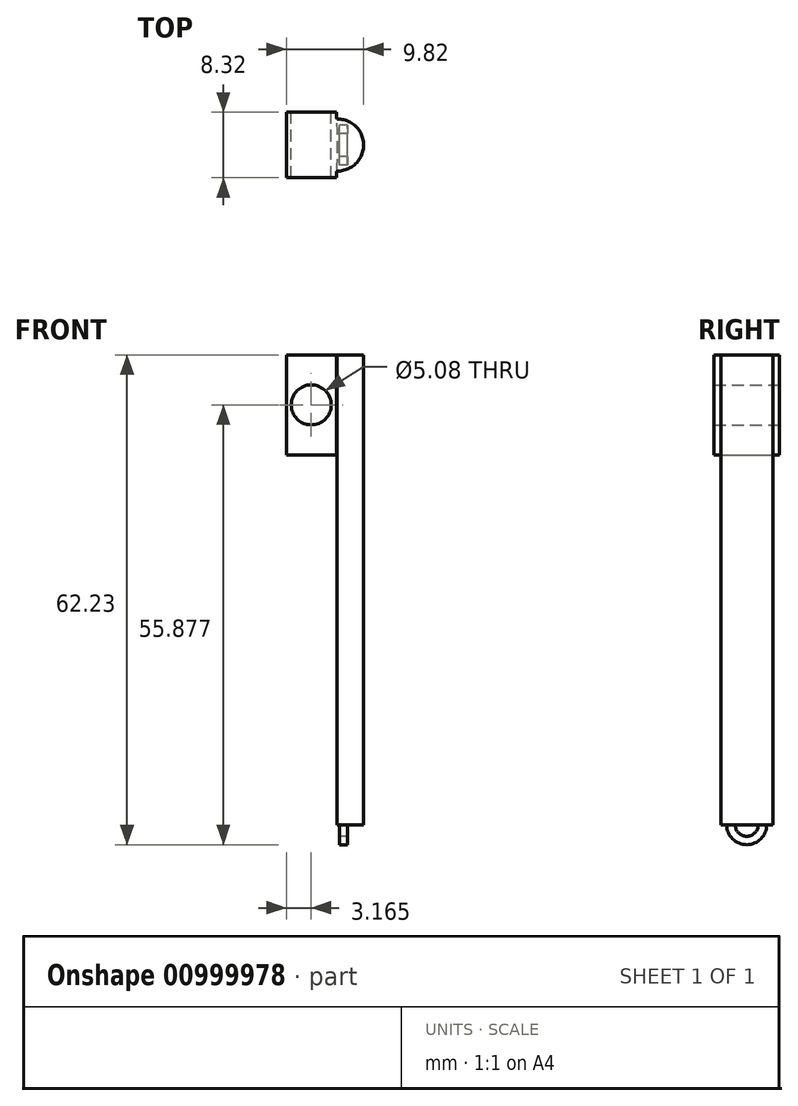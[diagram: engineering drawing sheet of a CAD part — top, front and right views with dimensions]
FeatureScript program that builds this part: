
annotation { "Feature Type Name" : "Feature", "Feature Type Description" : "" }
export const myFeature = defineFeature(function(context is Context, id is Id, definition is map)
    precondition{}
    {
        {
            var Q0;
            Q0=qCreatedBy(makeId("Top.planeOp"),FACE);
            var sketch = newSketch(context, id + "F0", { "sketchPlane" : qUnion([Q0])});
            skArc(sketch, "E0", {"start": v(50.7, -3.3) * mm, "mid": v(50.8, 0) * mm, "end": v(50.7, 3.3) * mm});
            skArc(sketch, "E1", {"start": v(50.7, -3.3) * mm, "mid": v(54.1, 0) * mm, "end": v(50.7, 3.3) * mm});
            skSolve(sketch);
        }
        {
            var Q0;
            Q0=makeQuery(id+"F0.imprint","IMPRINT",FACE,{"disambiguationData":[TD([[makeQuery(id+"F0.imprint","IMPRINT",EDGE,{"derivedFrom":sQuery(id+"F0.wireOp",EDGE,"E0")}),-1.0]])]});
            extrude(context, id + "F1", {"entities" : qUnion([Q0]), "depth" : 59.69 * mm, "offsetDistance" : 25.4 * mm});
        }
        {
            var Q0;
            Q0=makeQuery(id+"F1.opExtrude","CAP_FACE",FACE,{"disambiguationData":[OSD([sQuery(id+"F0.wireOp",EDGE,"E0"),sQuery(id+"F0.wireOp",EDGE,"E1")])],"isStart":false});
            var sketch = newSketch(context, id + "F2", { "sketchPlane" : qUnion([Q0])});
            skArc(sketch, "E2", {"start": v(50.63, -4.16) * mm, "mid": v(50.8, 0) * mm, "end": v(50.63, 4.16) * mm});
            skLineSegment(sketch, "E3", {"start": v(50.63, -4.16) * mm, "end": v(44.28, -4.16) * mm});
            skLineSegment(sketch, "E4", {"start": v(44.28, -4.16) * mm, "end": v(44.28, 4.16) * mm});
            skLineSegment(sketch, "E5", {"start": v(50.63, 4.16) * mm, "end": v(44.28, 4.16) * mm});
            skPoint(sketch, "E6.center.orphan", {"position": v(50.8, 0) * mm});
            skSolve(sketch);
        }
        {
            var Q0;
            Q0 = qSketchRegion(id + "F2", true);
            extrude(context, id + "F3", {"entities" : qUnion([Q0]), "operationType" : NewBodyOperationType.ADD, "oppositeDirection" : true, "depth" : 12.7 * mm, "offsetDistance" : 25.4 * mm});
        }
        {
            var Q0;
            Q0=makeQuery(id+"F3.opExtrude","SWEPT_FACE",FACE,{"disambiguationData":[OSD([sQuery(id+"F2.wireOp",EDGE,"E5")])]});
            var sketch = newSketch(context, id + "F4", { "sketchPlane" : qUnion([Q0])});
            skPoint(sketch, "E7.centerSnap0", {"position": v(-50.63, 53.34) * mm});
            skPoint(sketch, "E7.centerSnap1", {"position": v(-47.45, 59.7) * mm});
            skPoint(sketch, "E7.center.orphan", {"position": v(-47.45, 53.34) * mm});
            skSolve(sketch);
        }
        {
            var Q0;
            {var subQ0=sQuery(id+"F2.wireOp",EDGE,"E5");Q0=makeQuery(id+"F4.imprint","IMPRINT",FACE,{"disambiguationData":[TD([[makeQuery(id+"F4.imprint","IMPRINT",EDGE,{"derivedFrom":makeQuery(id+"F3.opExtrude","CAP_EDGE",EDGE,{"disambiguationData":[OSD([subQ0])],"isStart":true})}),-1.0]])]});}
            var sketch = newSketch(context, id + "F5", { "sketchPlane" : qUnion([Q0])});
            skCircle(sketch, "E8", {"center": v(-47.45, 53.34) * mm, "radius": 2.54 * mm});
            skSolve(sketch);
        }
        {
            var Q0;
            Q0 = qSketchRegion(id + "F5", true);
            extrude(context, id + "F6", {"entities" : qUnion([Q0]), "operationType" : NewBodyOperationType.REMOVE, "oppositeDirection" : true, "depth" : 25.4 * mm, "offsetDistance" : 25.4 * mm});
        }
        {
            var Q0;
            Q0=qCreatedBy(makeId("Right.planeOp"),FACE);
            var sketch = newSketch(context, id + "F7", { "sketchPlane" : qUnion([Q0])});
            skArc(sketch, "E9", {"start": v(-1.47, 0) * mm, "mid": v(0, -1.47) * mm, "end": v(1.47, 0) * mm});
            skArc(sketch, "E10", {"start": v(-2.54, 0) * mm, "mid": v(0, -2.54) * mm, "end": v(2.54, 0) * mm});
            skLineSegment(sketch, "E11", {"start": v(-1.47, 0) * mm, "end": v(-2.54, 0) * mm});
            skPoint(sketch, "E12.orphan", {"position": v(3.84, 0) * mm});
            skLineSegment(sketch, "E13", {"start": v(2.54, 0) * mm, "end": v(1.47, 0) * mm});
            skSolve(sketch);
        }
        {
            var Q0;
            Q0 = qSketchRegion(id + "F7", true);
            extrude(context, id + "F8", {"entities" : qUnion([Q0]), "operationType" : NewBodyOperationType.ADD, "depth" : 52.07 * mm, "offsetDistance" : 25.4 * mm});
        }
        {
            var Q0;
            Q0=qCreatedBy(makeId("Top.planeOp"),FACE);
            var sketch = newSketch(context, id + "F9", { "sketchPlane" : qUnion([Q0])});
            skLineSegment(sketch, "E14", {"start": v(51.03, -2.76) * mm, "end": v(51.03, 2.83) * mm});
            skLineSegment(sketch, "E15", {"start": v(51.03, -2.76) * mm, "end": v(-24.66, -2.76) * mm});
            skLineSegment(sketch, "E16", {"start": v(51.03, 2.83) * mm, "end": v(-24.66, 2.83) * mm});
            skLineSegment(sketch, "E17", {"start": v(-24.66, -2.76) * mm, "end": v(-24.66, 2.83) * mm});
            skSolve(sketch);
        }
        {
            var Q0;
            Q0 = qSketchRegion(id + "F9", true);
            extrude(context, id + "F10", {"entities" : qUnion([Q0]), "operationType" : NewBodyOperationType.REMOVE, "oppositeDirection" : true, "depth" : 25.4 * mm, "offsetDistance" : 25.4 * mm});
        }
    });
